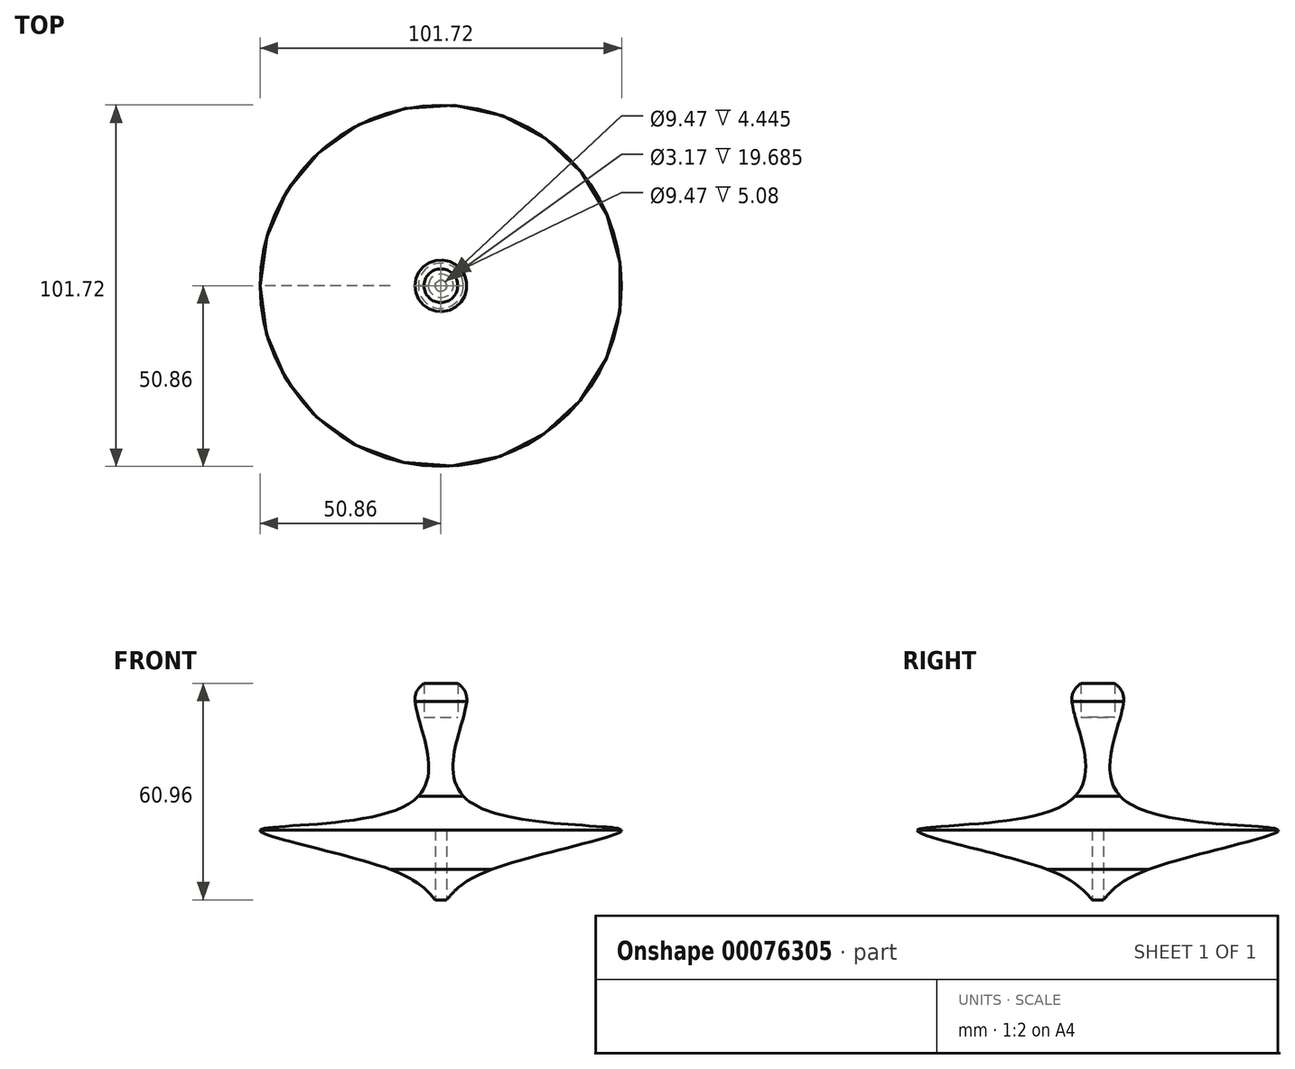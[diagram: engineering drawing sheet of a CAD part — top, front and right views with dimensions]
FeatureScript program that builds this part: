
annotation { "Feature Type Name" : "Feature", "Feature Type Description" : "" }
export const myFeature = defineFeature(function(context is Context, id is Id, definition is map)
    precondition{}
    {
        {
            var Q0;
            Q0=qCreatedBy(makeId("Front.planeOp"),FACE);
            var sketch = newSketch(context, id + "F0", { "sketchPlane" : qUnion([Q0])});
            skLineSegment(sketch, "E0", {"start": v(0, 0) * mm, "end": v(0, 63.5) * mm});
            skLineSegment(sketch, "E1", {"start": v(-1.59, 0) * mm, "end": v(-1.59, 22.23) * mm});
            skLineSegment(sketch, "E2", {"start": v(-1.59, 0) * mm, "end": v(-1.59, 2.54) * mm});
            skLineSegment(sketch, "E3", {"start": v(-1.59, 22.23) * mm, "end": v(0, 22.23) * mm});
            skLineSegment(sketch, "E4", {"start": v(0, 22.23) * mm, "end": v(-1.59, 22.23) * mm});
            skLineSegment(sketch, "E5", {"start": v(0, 22.23) * mm, "end": v(-50.8, 22.23) * mm});
            skLineSegment(sketch, "E6", {"start": v(-1.59, 11.11) * mm, "end": v(-14.29, 11.11) * mm});
            skPoint(sketch, "E7.3.internal.snap0", {"position": v(-1.59, 1.27) * mm});
            skLineSegment(sketch, "E8", {"start": v(-4.73, 63.5) * mm, "end": v(-4.73, 63.5) * mm});
            skLineSegment(sketch, "E9", {"start": v(-1.59, 0) * mm, "end": v(-63.5, 0) * mm});
            skPoint(sketch, "E10.visualSharp", {"position": v(-9.81, 63.5) * mm});
            skPoint(sketch, "E11.orphan", {"position": v(-9.81, 0) * mm});
            skLineSegment(sketch, "E12", {"start": v(-4.73, 63.5) * mm, "end": v(-4.73, 53.98) * mm});
            skLineSegment(sketch, "E13", {"start": v(-4.73, 53.98) * mm, "end": v(0, 53.98) * mm});
            skPoint(sketch, "E7.3.internal.orphan", {"position": v(-1.59, 37.1) * mm});
            skLineSegment(sketch, "E14", {"start": v(0, 0) * mm, "end": v(0, 31.75) * mm});
            skLineSegment(sketch, "E15", {"start": v(0, 31.75) * mm, "end": v(-6.35, 31.75) * mm});
            skFitSpline(sketch, "E16", {"points": [v(-1.59, 2.54) * mm, v(-14.29, 11.11) * mm, v(-50.8, 22.23) * mm, v(-6.35, 31.75) * mm, v(-9.81, 58.42) * mm, v(-4.73, 63.5) * mm], "startDerivative": vector(-46.05, 53.65) * mm, "endDerivative": vector(70.38, 27.87) * mm});
            skLineSegment(sketch, "E17", {"start": v(-4.73, 58.42) * mm, "end": v(-7.27, 58.42) * mm});
            skFitSpline(sketch, "E18", {"points": [v(-1.59, 2.54) * mm, v(-14.29, 11.11) * mm, v(-50.8, 22.23) * mm, v(-6.35, 31.75) * mm, v(-7.27, 58.42) * mm, v(-4.73, 63.5) * mm], "startDerivative": vector(-45.8, 52.94) * mm, "endDerivative": vector(41.58, 35.51) * mm});
            skLineSegment(sketch, "E19.trimOffspring", {"start": v(-6.35, 31.75) * mm, "end": v(-6.35, 31.75) * mm});
            skSolve(sketch);
        }
        {
            var Q0;
            {var subQ1=sQuery(id+"F0.wireOp",EDGE,"E12");Q0=makeQuery(id+"F0.imprint","IMPRINT",FACE,{"disambiguationData":[TD([[makeQuery(id+"F0.imprint","IMPRINT",EDGE,{"derivedFrom":subQ1}),-1.0]])]});}
            var Q1;
            {var subQ0=sQuery(id+"F0.wireOp",EDGE,"E15");Q1=makeQuery(id+"F0.imprint","IMPRINT",FACE,{"disambiguationData":[TD([[makeQuery(id+"F0.imprint","IMPRINT",EDGE,{"derivedFrom":subQ0}),1.0]])]});}
            var Q2;
            {var subQ3=sQuery(id+"F0.wireOp",EDGE,"E6");Q2=makeQuery(id+"F0.imprint","IMPRINT",FACE,{"disambiguationData":[TD([[makeQuery(id+"F0.imprint","IMPRINT",EDGE,{"derivedFrom":subQ3}),-1.0]])]});}
            var Q3;
            {var subQ3=sQuery(id+"F0.wireOp",EDGE,"E6");Q3=makeQuery(id+"F0.imprint","IMPRINT",FACE,{"disambiguationData":[TD([[makeQuery(id+"F0.imprint","IMPRINT",EDGE,{"derivedFrom":subQ3}),1.0]])]});}
            var Q4;
            Q4=sQuery(id+"F0.wireOp",EDGE,"E0");
            revolve(context, id + "F1", {"entities" : qUnion([Q0, Q1, Q2, Q3]), "axis" : qUnion([Q4]), "revolveType" : RevolveType.FULL});
        }
        {
            var Q0;
            {var subQ1=sQuery(id+"F0.wireOp",EDGE,"E13");Q0=makeQuery(id+"F0.imprint","IMPRINT",FACE,{"disambiguationData":[TD([[makeQuery(id+"F0.imprint","IMPRINT",EDGE,{"derivedFrom":subQ1}),-1.0]])]});}
            var Q1;
            Q1=sQuery(id+"F0.wireOp",EDGE,"E0");
            revolve(context, id + "F2", {"entities" : qUnion([Q0]), "axis" : qUnion([Q1]), "revolveType" : RevolveType.FULL});
        }
    });
